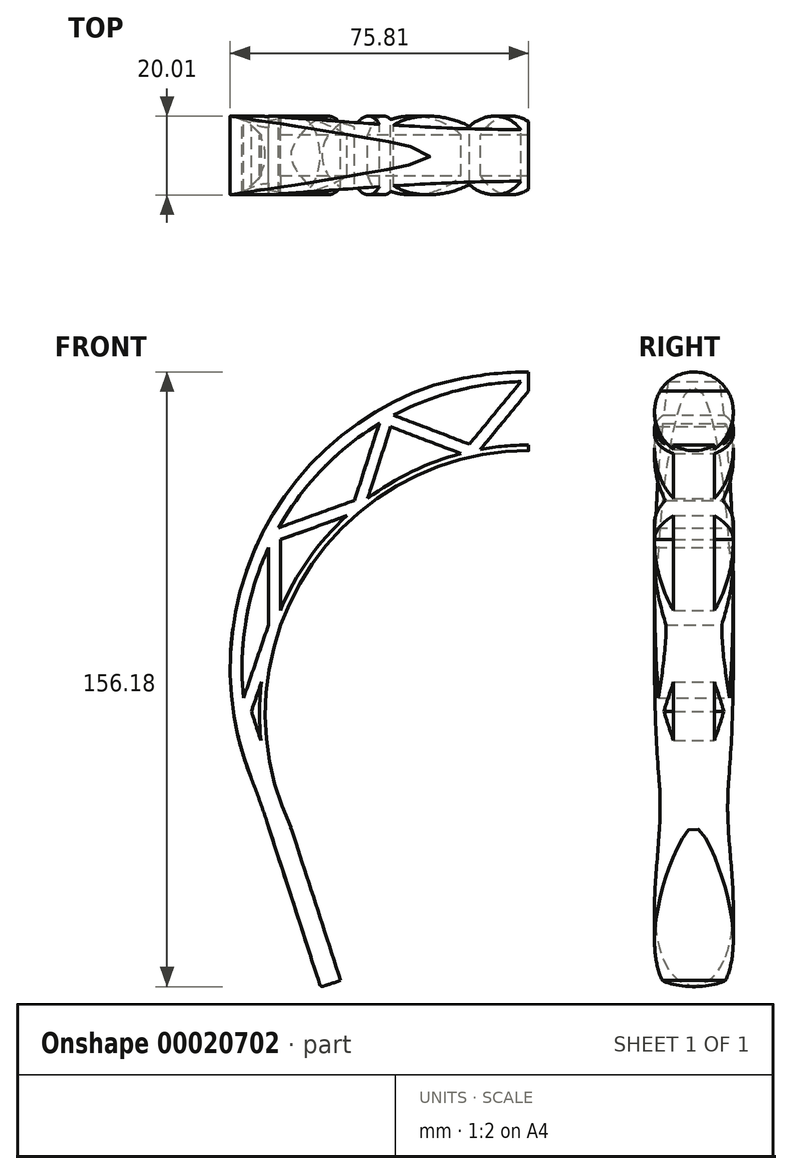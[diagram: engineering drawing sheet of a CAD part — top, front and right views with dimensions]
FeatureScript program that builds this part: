
annotation { "Feature Type Name" : "Feature", "Feature Type Description" : "" }
export const myFeature = defineFeature(function(context is Context, id is Id, definition is map)
    precondition{}
    {
        {
            var Q0;
            Q0=qCreatedBy(makeId("Front.planeOp"),FACE);
            var sketch = newSketch(context, id + "F0", { "sketchPlane" : qUnion([Q0])});
            skCircle(sketch, "E0.cCircle", {"center": v(0, 0) * mm, "radius": 68.35 * mm, "construction": true});
            skLineSegment(sketch, "E0.0", {"start": v(49.66, -68.35) * mm, "end": v(-49.66, -68.35) * mm});
            skLineSegment(sketch, "E0.1", {"start": v(-49.66, -68.35) * mm, "end": v(-80.34, 26.1) * mm});
            skLineSegment(sketch, "E0.2", {"start": v(-80.34, 26.1) * mm, "end": v(0, 84.48) * mm});
            skLineSegment(sketch, "E0.3", {"start": v(0, 84.48) * mm, "end": v(80.34, 26.1) * mm});
            skLineSegment(sketch, "E0.4", {"start": v(80.34, 26.1) * mm, "end": v(49.66, -68.35) * mm});
            skPoint(sketch, "E0.0.midPoint", {"position": v(0, -68.35) * mm});
            skLineSegment(sketch, "E1", {"start": v(-80.34, 26.1) * mm, "end": v(65, -21.12) * mm, "construction": true});
            skLineSegment(sketch, "E2", {"start": v(-65, -21.12) * mm, "end": v(80.34, 26.1) * mm, "construction": true});
            skLineSegment(sketch, "E3", {"start": v(0, 84.48) * mm, "end": v(-49.66, -68.35) * mm, "construction": true});
            skLineSegment(sketch, "E4", {"start": v(80.34, 26.1) * mm, "end": v(-49.66, -68.35) * mm, "construction": true});
            skLineSegment(sketch, "E5", {"start": v(-80.34, 26.1) * mm, "end": v(49.66, -68.35) * mm, "construction": true});
            skLineSegment(sketch, "E6", {"start": v(80.34, 26.1) * mm, "end": v(-80.34, 26.1) * mm, "construction": true});
            skLineSegment(sketch, "E7", {"start": v(0, 84.48) * mm, "end": v(49.66, -68.35) * mm, "construction": true});
            skSolve(sketch);
        }
        {
            var Q0;
            Q0=qCreatedBy(makeId("Front.planeOp"),FACE);
            var sketch = newSketch(context, id + "F1", { "sketchPlane" : qUnion([Q0])});
            skArc(sketch, "E8.0", {"start": v(65, -21.12) * mm, "mid": v(0, 68.35) * mm, "end": v(-65, -21.12) * mm});
            skPoint(sketch, "E9", {"position": v(0, -32.27) * mm});
            skLineSegment(sketch, "E10", {"start": v(-65, -21.12) * mm, "end": v(-49.66, -68.35) * mm});
            skLineSegment(sketch, "E11", {"start": v(65, -21.12) * mm, "end": v(49.66, -68.35) * mm});
            skSolve(sketch);
        }
        {
            var Q0;
            Q0=qCreatedBy(makeId("Front.planeOp"),FACE);
            var sketch = newSketch(context, id + "F2", { "sketchPlane" : qUnion([Q0])});
            skArc(sketch, "E12", {"start": v(0, 68.35) * mm, "mid": v(-55.73, 39.56) * mm, "end": v(-64.52, -22.54) * mm});
            skArc(sketch, "E13", {"start": v(1.5, 84.46) * mm, "mid": v(-61.6, 50.47) * mm, "end": v(-65, -21.12) * mm});
            skArc(sketch, "E14.0", {"start": v(0, 66.35) * mm, "mid": v(-53.67, 39) * mm, "end": v(-63.1, -20.5) * mm});
            skArc(sketch, "E15.0", {"start": v(0, 87.48) * mm, "mid": v(-62.66, 54.34) * mm, "end": v(-70.53, -16.1) * mm});
            skLineSegment(sketch, "E16", {"start": v(-65, -21.12) * mm, "end": v(-71.98, 0.72) * mm});
            skLineSegment(sketch, "E17", {"start": v(-71.98, 0.72) * mm, "end": v(-64.56, 22.42) * mm});
            skLineSegment(sketch, "E18", {"start": v(-64.56, 22.42) * mm, "end": v(-64.55, 45.35) * mm});
            skLineSegment(sketch, "E19", {"start": v(-64.55, 45.35) * mm, "end": v(-42.99, 53.13) * mm});
            skLineSegment(sketch, "E20", {"start": v(-42.99, 53.13) * mm, "end": v(-35.98, 74.97) * mm});
            skLineSegment(sketch, "E21", {"start": v(-35.98, 74.97) * mm, "end": v(-14.57, 66.77) * mm});
            skLineSegment(sketch, "E22", {"start": v(-14.57, 66.77) * mm, "end": v(0, 84.48) * mm});
            skArc(sketch, "E23.0.startCap", {"start": v(-63.06, 22.42) * mm, "mid": v(-64.56, 20.92) * mm, "end": v(-66.06, 22.42) * mm});
            skArc(sketch, "E23.0.endCap", {"start": v(-66.05, 45.35) * mm, "mid": v(-64.55, 46.85) * mm, "end": v(-63.05, 45.34) * mm});
            skLineSegment(sketch, "E23.0.left", {"start": v(-66.06, 22.42) * mm, "end": v(-66.05, 45.35) * mm});
            skLineSegment(sketch, "E23.0.right", {"start": v(-63.06, 22.42) * mm, "end": v(-63.05, 45.34) * mm});
            skArc(sketch, "E23.1.startCap", {"start": v(-64.04, 43.93) * mm, "mid": v(-65.96, 44.84) * mm, "end": v(-65.06, 46.76) * mm});
            skArc(sketch, "E23.1.endCap", {"start": v(-43.5, 54.54) * mm, "mid": v(-41.58, 53.64) * mm, "end": v(-42.48, 51.72) * mm});
            skLineSegment(sketch, "E23.1.left", {"start": v(-65.06, 46.76) * mm, "end": v(-43.5, 54.54) * mm});
            skLineSegment(sketch, "E23.1.right", {"start": v(-64.04, 43.93) * mm, "end": v(-42.48, 51.72) * mm});
            skArc(sketch, "E24.0.startCap", {"start": v(-41.56, 52.68) * mm, "mid": v(-43.44, 51.7) * mm, "end": v(-44.41, 53.6) * mm});
            skArc(sketch, "E24.0.endCap", {"start": v(-37.41, 75.42) * mm, "mid": v(-35.52, 76.4) * mm, "end": v(-34.55, 74.5) * mm});
            skLineSegment(sketch, "E24.0.left", {"start": v(-44.41, 53.6) * mm, "end": v(-37.41, 75.42) * mm});
            skLineSegment(sketch, "E24.0.right", {"start": v(-41.56, 52.68) * mm, "end": v(-34.55, 74.5) * mm});
            skArc(sketch, "E24.1.startCap", {"start": v(-36.52, 73.56) * mm, "mid": v(-37.38, 75.5) * mm, "end": v(-35.45, 76.37) * mm});
            skArc(sketch, "E24.1.endCap", {"start": v(-14.03, 68.18) * mm, "mid": v(-13.17, 66.24) * mm, "end": v(-15.1, 65.37) * mm});
            skLineSegment(sketch, "E24.1.left", {"start": v(-35.45, 76.37) * mm, "end": v(-14.03, 68.18) * mm});
            skLineSegment(sketch, "E24.1.right", {"start": v(-36.52, 73.56) * mm, "end": v(-15.1, 65.37) * mm});
            skArc(sketch, "E24.2.startCap", {"start": v(-13.4, 65.82) * mm, "mid": v(-15.52, 65.62) * mm, "end": v(-15.73, 67.73) * mm});
            skArc(sketch, "E24.2.endCap", {"start": v(-1.16, 85.43) * mm, "mid": v(0.95, 85.64) * mm, "end": v(1.16, 83.53) * mm});
            skLineSegment(sketch, "E24.2.left", {"start": v(-15.73, 67.73) * mm, "end": v(-1.16, 85.43) * mm});
            skLineSegment(sketch, "E24.2.right", {"start": v(-13.4, 65.82) * mm, "end": v(1.16, 83.53) * mm});
            skArc(sketch, "E24.3.startCap", {"start": v(-70.56, 0.24) * mm, "mid": v(-72.46, -0.7) * mm, "end": v(-73.4, 1.2) * mm});
            skArc(sketch, "E24.3.endCap", {"start": v(-65.98, 22.9) * mm, "mid": v(-64.08, 23.84) * mm, "end": v(-63.14, 21.93) * mm});
            skLineSegment(sketch, "E24.3.left", {"start": v(-73.4, 1.2) * mm, "end": v(-65.98, 22.9) * mm});
            skLineSegment(sketch, "E24.3.right", {"start": v(-70.56, 0.24) * mm, "end": v(-63.14, 21.93) * mm});
            skArc(sketch, "E24.4.startCap", {"start": v(-63.57, -20.66) * mm, "mid": v(-64.54, -22.55) * mm, "end": v(-66.43, -21.58) * mm});
            skArc(sketch, "E24.4.endCap", {"start": v(-73.4, 0.26) * mm, "mid": v(-72.43, 2.15) * mm, "end": v(-70.55, 1.18) * mm});
            skLineSegment(sketch, "E24.4.left", {"start": v(-66.43, -21.58) * mm, "end": v(-73.4, 0.26) * mm});
            skLineSegment(sketch, "E24.4.right", {"start": v(-63.57, -20.66) * mm, "end": v(-70.55, 1.18) * mm});
            skLineSegment(sketch, "E25", {"start": v(0, 87.48) * mm, "end": v(0, 66.35) * mm});
            skLineSegment(sketch, "E26", {"start": v(-66.41, -27.57) * mm, "end": v(-52.83, -69.38) * mm});
            skLineSegment(sketch, "E27", {"start": v(-63.1, -20.5) * mm, "end": v(-47.75, -67.73) * mm});
            skLineSegment(sketch, "E28", {"start": v(-52.83, -69.38) * mm, "end": v(-47.75, -67.73) * mm});
            skPoint(sketch, "E29.visualSharp", {"position": v(-68.89, -19.96) * mm});
            skArc(sketch, "E29.filletArc", {"start": v(-66.41, -27.57) * mm, "mid": v(-68.39, -21.8) * mm, "end": v(-70.53, -16.1) * mm});
            skSolve(sketch);
        }
        {
            var Q0;
            Q0=qCreatedBy(makeId("Front.planeOp"),FACE);
            var sketch = newSketch(context, id + "F3", { "sketchPlane" : qUnion([Q0])});
            skArc(sketch, "E30.0", {"start": v(0, 87.48) * mm, "mid": v(-62.66, 54.34) * mm, "end": v(-70.53, -16.1) * mm});
            skArc(sketch, "E30.1", {"start": v(-66.41, -27.57) * mm, "mid": v(-68.39, -21.8) * mm, "end": v(-70.53, -16.1) * mm});
            skLineSegment(sketch, "E30.2", {"start": v(-66.41, -27.57) * mm, "end": v(-52.83, -69.38) * mm});
            skLineSegment(sketch, "E30.3", {"start": v(-52.83, -69.38) * mm, "end": v(-47.75, -67.73) * mm});
            skLineSegment(sketch, "E30.4", {"start": v(-63.1, -20.5) * mm, "end": v(-47.75, -67.73) * mm});
            skArc(sketch, "E30.5", {"start": v(0, 66.35) * mm, "mid": v(-53.67, 39) * mm, "end": v(-63.1, -20.5) * mm});
            skLineSegment(sketch, "E30.6", {"start": v(0, 87.48) * mm, "end": v(0, 66.35) * mm});
            skSolve(sketch);
        }
        {
            var Q0;
            Q0 = qSketchRegion(id + "F3", true);
            extrude(context, id + "F4", {"entities" : qUnion([Q0]), "depth" : 10 * mm});
        }
        {
            var Q0;
            {var subQ0=sQuery(id+"F2.wireOp",EDGE,"E24.2.left");var subQ3=sQuery(id+"F2.wireOp",EDGE,"E13");var subQ4=makeQuery(id+"F2.imprint","INTERSECT",VERTEX,{"derivedFrom":[subQ3,subQ0]});Q0=makeQuery(id+"F2.imprint","IMPRINT",FACE,{"disambiguationData":[TD([[makeQuery(id+"F2.imprint","IMPRINT",EDGE,{"disambiguationData":[TD([[subQ4,-1.0]])],"derivedFrom":subQ3}),1.0]])]});}
            var Q1;
            {var subQ0=sQuery(id+"F2.wireOp",EDGE,"E25");var subQ3=sQuery(id+"F2.wireOp",EDGE,"E12");var subQ4=makeQuery(id+"F2.imprint","INTERSECT",VERTEX,{"derivedFrom":[subQ3,subQ0]});Q1=makeQuery(id+"F2.imprint","IMPRINT",FACE,{"disambiguationData":[TD([[makeQuery(id+"F2.imprint","IMPRINT",EDGE,{"disambiguationData":[TD([[subQ4,-1.0]])],"derivedFrom":subQ3}),-1.0]])]});}
            var Q2;
            {var subQ0=sQuery(id+"F2.wireOp",EDGE,"E24.1.right");var subQ3=sQuery(id+"F2.wireOp",EDGE,"E12");var subQ4=makeQuery(id+"F2.imprint","INTERSECT",VERTEX,{"derivedFrom":[subQ3,subQ0]});Q2=makeQuery(id+"F2.imprint","IMPRINT",FACE,{"disambiguationData":[TD([[makeQuery(id+"F2.imprint","IMPRINT",EDGE,{"disambiguationData":[TD([[subQ4,-1.0]])],"derivedFrom":subQ3}),-1.0]])]});}
            var Q3;
            {var subQ0=sQuery(id+"F2.wireOp",EDGE,"E24.0.left");var subQ3=sQuery(id+"F2.wireOp",EDGE,"E13");var subQ4=makeQuery(id+"F2.imprint","INTERSECT",VERTEX,{"derivedFrom":[subQ3,subQ0]});Q3=makeQuery(id+"F2.imprint","IMPRINT",FACE,{"disambiguationData":[TD([[makeQuery(id+"F2.imprint","IMPRINT",EDGE,{"disambiguationData":[TD([[subQ4,-1.0]])],"derivedFrom":subQ3}),1.0]])]});}
            var Q4;
            {var subQ0=sQuery(id+"F2.wireOp",EDGE,"E23.1.right");var subQ3=sQuery(id+"F2.wireOp",EDGE,"E12");var subQ4=makeQuery(id+"F2.imprint","INTERSECT",VERTEX,{"derivedFrom":[subQ3,subQ0]});Q4=makeQuery(id+"F2.imprint","IMPRINT",FACE,{"disambiguationData":[TD([[makeQuery(id+"F2.imprint","IMPRINT",EDGE,{"disambiguationData":[TD([[subQ4,-1.0]])],"derivedFrom":subQ3}),-1.0]])]});}
            var Q5;
            {var subQ1=sQuery(id+"F2.wireOp",EDGE,"E23.0.left");var subQ3=sQuery(id+"F2.wireOp",EDGE,"E13");var subQ5=makeQuery(id+"F2.imprint","INTERSECT",VERTEX,{"derivedFrom":[subQ3,subQ1]});Q5=makeQuery(id+"F2.imprint","IMPRINT",FACE,{"disambiguationData":[TD([[makeQuery(id+"F2.imprint","IMPRINT",EDGE,{"disambiguationData":[TD([[subQ5,-1.0]])],"derivedFrom":subQ3}),1.0]])]});}
            var Q6;
            {var subQ1=sQuery(id+"F2.wireOp",EDGE,"E24.3.right");var subQ3=sQuery(id+"F2.wireOp",EDGE,"E12");var subQ5=makeQuery(id+"F2.imprint","INTERSECT",VERTEX,{"derivedFrom":[subQ3,subQ1]});Q6=makeQuery(id+"F2.imprint","IMPRINT",FACE,{"disambiguationData":[TD([[makeQuery(id+"F2.imprint","IMPRINT",EDGE,{"disambiguationData":[TD([[subQ5,-1.0]])],"derivedFrom":subQ3}),-1.0]])]});}
            extrude(context, id + "F5", {"entities" : qUnion([Q0, Q1, Q2, Q3, Q4, Q5, Q6]), "operationType" : NewBodyOperationType.REMOVE, "endBound" : BoundingType.THROUGH_ALL, "depth" : 25 * mm});
        }
        {
            var Q0;
            Q0=qCreatedBy(makeId("Right.planeOp"),FACE);
            var sketch = newSketch(context, id + "F6", { "sketchPlane" : qUnion([Q0])});
            skCircle(sketch, "E31", {"center": v(0, 76.91) * mm, "radius": 10 * mm});
            skSolve(sketch);
        }
        {
            var Q0;
            Q0=qCreatedBy(makeId("Right.planeOp"),FACE);
            var sketch = newSketch(context, id + "F7", { "sketchPlane" : qUnion([Q0])});
            skLineSegment(sketch, "E32", {"start": v(-57.2, 0) * mm, "end": v(0, 0) * mm});
            skSolve(sketch);
        }
        {
            var Q0;
            Q0=makeQuery(id+"F4.opExtrude","SWEPT_BODY",BODY,{"disambiguationData":[OSD([sQuery(id+"F3.wireOp",EDGE,"E30.0"),sQuery(id+"F3.wireOp",EDGE,"E30.1"),sQuery(id+"F3.wireOp",EDGE,"E30.2"),sQuery(id+"F3.wireOp",EDGE,"E30.3"),sQuery(id+"F3.wireOp",EDGE,"E30.4"),sQuery(id+"F3.wireOp",EDGE,"E30.5"),sQuery(id+"F3.wireOp",EDGE,"E30.6")])]});
            var Q1;
            Q1=qCreatedBy(makeId("Front.planeOp"),FACE);
            mirror(context, id + "F8", {"operationType" : NewBodyOperationType.ADD, "entities" : qUnion([Q0]), "mirrorPlane" : qUnion([Q1])});
        }
        {
            var Q0;
            Q0=makeQuery(id+"F4.opExtrude","SWEPT_BODY",BODY,{"disambiguationData":[OSD([sQuery(id+"F3.wireOp",EDGE,"E30.0"),sQuery(id+"F3.wireOp",EDGE,"E30.1"),sQuery(id+"F3.wireOp",EDGE,"E30.2"),sQuery(id+"F3.wireOp",EDGE,"E30.3"),sQuery(id+"F3.wireOp",EDGE,"E30.4"),sQuery(id+"F3.wireOp",EDGE,"E30.5"),sQuery(id+"F3.wireOp",EDGE,"E30.6")])]});
            var Q1;
            Q1=qCreatedBy(makeId("Right.planeOp"),FACE);
            mirror(context, id + "F9", {"operationType" : NewBodyOperationType.ADD, "entities" : qUnion([Q0]), "mirrorPlane" : qUnion([Q1])});
        }
        {
            var Q0;
            Q0=makeQuery(id+"F6.imprint","IMPRINT",FACE,{"disambiguationData":[TD([[makeQuery(id+"F6.imprint","IMPRINT",EDGE,{"derivedFrom":sQuery(id+"F6.wireOp",EDGE,"E31")}),1.0]])]});
            var Q1;
            Q1=sQuery(id+"F7.wireOp",EDGE,"E32");
            revolve(context, id + "F10", {"operationType" : NewBodyOperationType.INTERSECT, "entities" : qUnion([Q0]), "axis" : qUnion([Q1]), "revolveType" : RevolveType.ONE_DIRECTION, "oppositeDirection" : true, "angle" : 150.44 * degree});
        }
    });
